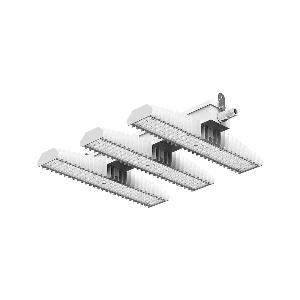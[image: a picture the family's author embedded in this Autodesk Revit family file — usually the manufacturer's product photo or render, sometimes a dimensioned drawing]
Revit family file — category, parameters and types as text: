
# Revit family: 3f_filippi_-_3f_lem_concentrato_3f_filippi_-_58907_-_3f_lem_3_led_150_dali_cr_conc
name_source: partatom
category: Lighting Fixtures
units: mm (PartAtom-declared; Revit-internal decimal feet)

## family parameters
Cut with Voids When Loaded = No
Host = Face
Light Source = No
Part Type = Normal
Room Calculation Point = No
Round Connector Dimension = Use Diameter
Shared = No

## types (1)
- 3F Filippi - 3F LEM Concentrato (1 x LED, 24405 lm, 165 W, 4000 K)
    Apparent Load = 165 VA
    Approval mark = CE
    CIE Flux Codes = 83 96 99 100 100
    Color Rendering = 80
    Color Temperature = 4000 K
    Control Gear = Electronic transformer
    Default Elevation = 1800 mm
    Description = Industrial luminaire with high light output and high luminous efficiency designed with the most innovative technologies for environments with temperature up to 55°C.

ILLUMINOTECHNICAL
Luminous efficiency 100% (DLOR 100%, ULOR 0%).
Initial luminous flux of the luminaire 24405 lm.
Direct symmetric narrow distribution: the illuminated area has a elliptical shape.
Installation Interdistance Transv.D = 0.52 x hu - Long.D = 1.16 x hu.
Tabular UGR (CIE 117 - 4H-8H; S=0.25H; 70/50/20): RUG 17.5 - 21.3.
Beam angle: 31° - 73°.
Luminous efficacy 148 lm/W.
Lifetime (L93/B10): 30000 h. (tq+25°C)
Lifetime (L90/B10): 50000 h. (tq+25°C)
Lifetime (L85/B10): 80000 h. (tq+25°C)
Lifetime (L80/B10): 100000 h. (tq+25°C)
Lifetime (L85/B10): 50000 h. (tq+55°C)
Sudden decreased luminous flux after 50000 hours: 0% (C0).
Photobiological safety in compliance with IEC/TR 62778: RG0 risk exempt, (IEC 62471).
In compliance with IEC/EN 62722-2-1 - IEC/EN 62717 standards.

SOURCE
3 Mid-Power linear LED modules 50W/840.
Energy efficiency class (UE 2019/2020 - UE 2019/2015): C.
CIE 13.3 Colour rendering index: CRI >80 (R9 <50%).
IES TM-30 Fidelity Index: Rf = 84 Rg = 95.
CCT nominal colour temperature 4000 K.
Colour initial tolerance (MacAdam): SDCM 3.

MECHANICAL
Passive modular heatsinks in die-casted aluminium, painted in white colour.
To optimize the thermal management of the LED module, the heatsinks are oversized and provided with self-cleaning of cooling fins.
Wiring body in aluminium and galvanised steel anchored solidly to the sinks and thermally separated.
3F Lens lenses with high luminous efficiency, transparent methacrylate (PMMA), fixed to the LED modules.
Fixing brackets in stainless steel.
Luminaire with limited surface temperature. - D - (EN 60598-2-24)
Dimensions: 657x542 mm, height 129 mm. Weight 14.4 kg.
IP65 protection degree.
Mechanical strength to impacts IK06 (1 joule).
Glow-wire test resistance 650°C.

ELECTRICAL
Halogen Free DALI-2 DATI (Parts 251, 252, 253), PUSH-DIM, electronic wiring 230V-50/60Hz, power factor 0.97 at full load, THD <25%, constant output current, class I, 2 driver, 2 DALI addresses.
Power of the luminaire 165 W.
ENEC - CE.
SAFE FLICKER: PstLM=<1 and SVM=<0.4 (IEC TR 61547-1 and IEC TR 63158), to ensure a more comfortable and safe light.
Luminaire compliant with EN 60598-2-22 for power supply from a centralised emergency system CPSS (Central Power Supply System), not incorporated in the luminaire - high risk areas excluded. The default power and flux are 100% in AC and 15% in DC.
Ambient temperature from -30°C to +55°C.
Temperature class T6 max 85°C.
Quick connection via M25 5P connector with 9-13 mm tightening range.
Power unit positioned on a separate compartment by the LED module to ensure optimum temperatures of cabling components, to be inspectable and maintainable.
Relative humidity UR: <85%.

INSTALLATION
Ceiling / Suspended / Wall.
All accessories dedicated to this product are available on the Catalog and on our website www.3F-Filippi.com.

APPLICATIONS
In commercial environments, exhibition and industrial areas, stores, open areas or with shelves.
Applications with high ambient temperature up to 55°C.
Environments in which it is necessary a total protection against falling fragments (eg environments with foodstuffs or machines with moving parts or with extreme temperature changes), use luminaires with polycarbonate lenses.

LIGHT MANAGEMENT
Recommended minimum setting: 10%.
The luminaire, equipped with (DALI-2 DATI) driver, can be controlled manually with 3F Easy Dim technology or automatically/manually with wired or wireless DALI/D2D control systems.
The D2D driver guarantees interoperability with other devices with the same certification by making the following information available:
Device Data (Part 251), Energy Report (Part 252), Diagnosis & Maintenance (Part 253).
In electrical systems without a regulation system (manual or automatic) and DALI bus, a suitable jumper must be made on the DA-DA terminals of the appliance.

WARNING
Fixture not suitable for cold stores with an ambient temperature <0°C and/or relative humidity >85%.
Luminaire designed for disposal/recycling at end-of-life.
Replaceable (LED only) light source by a professional. Replaceable control gear by a professional.
    Height = 129 mm
    Lamp = 1 x LED
    Lamp Light Flux = 24405 lm
    Lamp Power = 165 W
    Lamp count = 1
    Length = 657 mm
    Lifetime = 50000 h
    Luminous efficacy = 148 lm/W
    Manufacturer = 3F Filippi
    ModVariant = No
    Model = 3F Filippi - 58907 - 3F LEM 3 LED 150 DALI CR CONC
    Mounting Place = Ceiling
    Mounting Type = Pendant
    Number of Poles = 1
    OnlyDefault = Yes
    Power Factor = 1
    Product Name = 3F Filippi - 3F LEM Concentrato
    Product group = pendant luminaire
    ProductGroupID = 9
    Protection Class = Protection class I
    Protection Degree = IP 65
    RLX_Detail_Level = 1
    RLX_Emergency_Light_Flux = 0 lm
    RLX_Emergency_Type = 0
    RLX_Emergency_Type_DB = No
    RlxData = <blob elided: 103429 chars, md5=445b1581>
    Socket = socket
    Standby Power = 0 W
    System Light Flux = 24405 lm
    System Power = 165 W
    Type Comments = Product without accessories
    Type Image = 3f_filippi_-_lem_3.jpg
    URL = http://relux.com
    VarID = ---
    Voltage = 0 V
    Weight = 0.00 kg
    Width = 542 mm

## geometry (parser evidence)
native form markers: Blend x4, Sweep x11
no freeform markers — native parametric forms only
